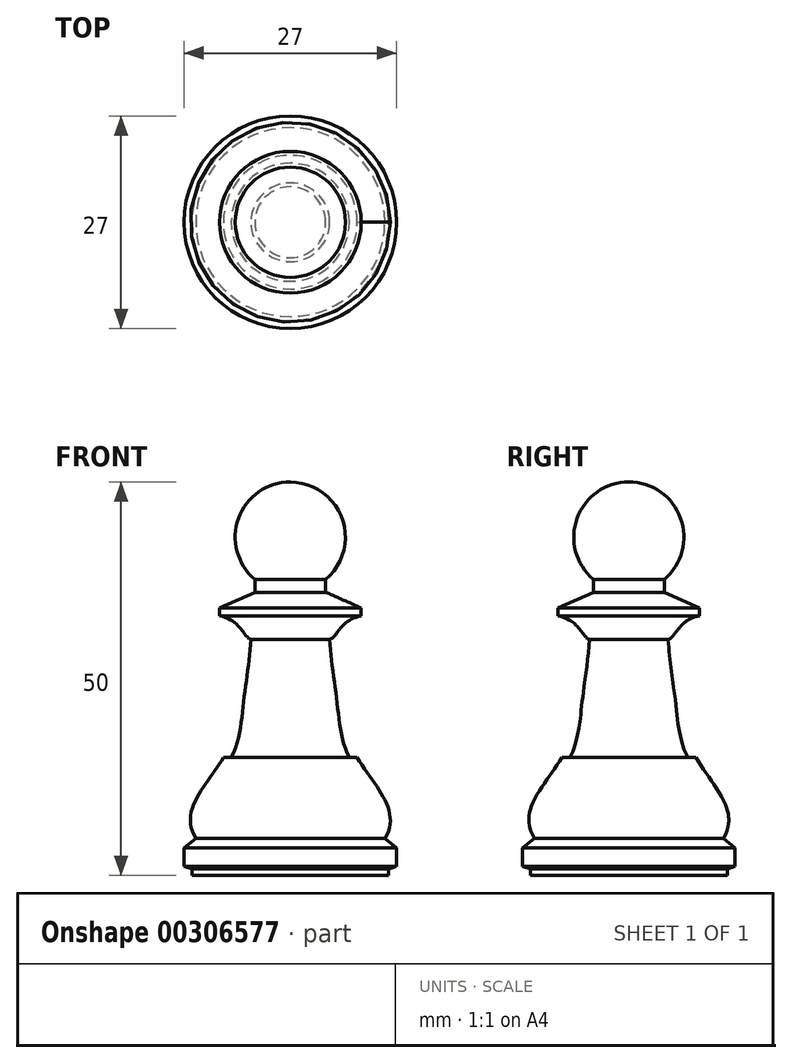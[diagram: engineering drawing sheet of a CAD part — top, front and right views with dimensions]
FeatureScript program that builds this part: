
annotation { "Feature Type Name" : "Feature", "Feature Type Description" : "" }
export const myFeature = defineFeature(function(context is Context, id is Id, definition is map)
    precondition{}
    {
        {
            var Q0;
            Q0=qCreatedBy(makeId("Front.planeOp"),FACE);
            var sketch = newSketch(context, id + "F0", { "sketchPlane" : qUnion([Q0])});
            skLineSegment(sketch, "E0", {"start": v(0, 51.57) * mm, "end": v(0, -41.13) * mm, "construction": true});
            skArc(sketch, "E1", {"start": v(4.5, 15.55) * mm, "mid": v(6.58, 23.3) * mm, "end": v(0, 27.92) * mm});
            skLineSegment(sketch, "E2", {"start": v(4.5, 15.55) * mm, "end": v(4.5, 13.92) * mm});
            skLineSegment(sketch, "E3", {"start": v(4.5, 13.92) * mm, "end": v(9, 11.92) * mm});
            skLineSegment(sketch, "E4", {"start": v(9, 11.92) * mm, "end": v(9, 10.92) * mm});
            skFitSpline(sketch, "E5", {"points": [v(9, 10.92) * mm, v(5, 7.92) * mm], "startDerivative": vector(-8.38, -1.69) * mm, "endDerivative": vector(-2.91, -0.7) * mm});
            skFitSpline(sketch, "E6", {"points": [v(5, 7.92) * mm, v(5.93, 0) * mm, v(7.5, -7.08) * mm], "startDerivative": vector(0.84, -15.02) * mm, "endDerivative": vector(6.91, -13.1) * mm});
            skLineSegment(sketch, "E7", {"start": v(7.5, -7.08) * mm, "end": v(8.5, -7.08) * mm});
            skFitSpline(sketch, "E8", {"points": [v(8.5, -7.08) * mm, v(12, -17.38) * mm], "startDerivative": vector(6.71, -11.1) * mm, "endDerivative": vector(-6.58, -10.75) * mm});
            skLineSegment(sketch, "E9", {"start": v(12, -17.38) * mm, "end": v(13.5, -18.57) * mm});
            skLineSegment(sketch, "E10", {"start": v(13.5, -18.57) * mm, "end": v(13.5, -20.9) * mm});
            skLineSegment(sketch, "E11", {"start": v(13.5, -20.9) * mm, "end": v(12.5, -21.26) * mm});
            skLineSegment(sketch, "E12", {"start": v(12.5, -21.26) * mm, "end": v(12.5, -22.08) * mm});
            skLineSegment(sketch, "E13", {"start": v(12.5, -22.08) * mm, "end": v(0, -22.08) * mm});
            skLineSegment(sketch, "E14", {"start": v(0, 27.92) * mm, "end": v(0, -22.08) * mm});
            skSolve(sketch);
        }
        {
            var Q0;
            Q0=makeQuery(id+"F0.imprint","IMPRINT",FACE,{"disambiguationData":[TD([[makeQuery(id+"F0.imprint","IMPRINT",EDGE,{"derivedFrom":sQuery(id+"F0.wireOp",EDGE,"E1")}),1.0]])]});
            var Q1;
            Q1=sQuery(id+"F0.wireOp",EDGE,"E0");
            revolve(context, id + "F1", {"entities" : qUnion([Q0]), "axis" : qUnion([Q1]), "revolveType" : RevolveType.FULL});
        }
    });
